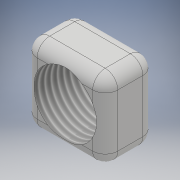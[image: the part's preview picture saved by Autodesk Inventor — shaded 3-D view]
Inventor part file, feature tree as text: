
AUTODESK INVENTOR PART (.ipt)
format: ipt  version: 2017 (Build 210142000, 142)  size: 151,040 bytes
history: native  units: mm
features: extrude x1, fillet x1, thread x1, sketch x1
ambient origin geometry x8: Origin, YZ Plane, XZ Plane, XY Plane, X Axis, Y Axis, Z Axis, Center Point
bodies: Solid1 (feature_tree)
feature tree (4):
  extrude  "Extrusion1"  Depth=10.0mm TaperAngle=0.0deg
  fillet  "Fillet1"  Radius=2.0mm
  thread  "Thread1"  [1 undecoded]
  sketch  "Sketch1"  dims[d0=10.0mm d1=8.0mm d2=0.0mm d3=2.0mm d4=10.0mm d5=0.0mm]
note: 1 required parameter value undecoded (feature->parameter linkage not recoverable at this tier; creation-order binding heuristic only, values carry confidence <= 0.55)
